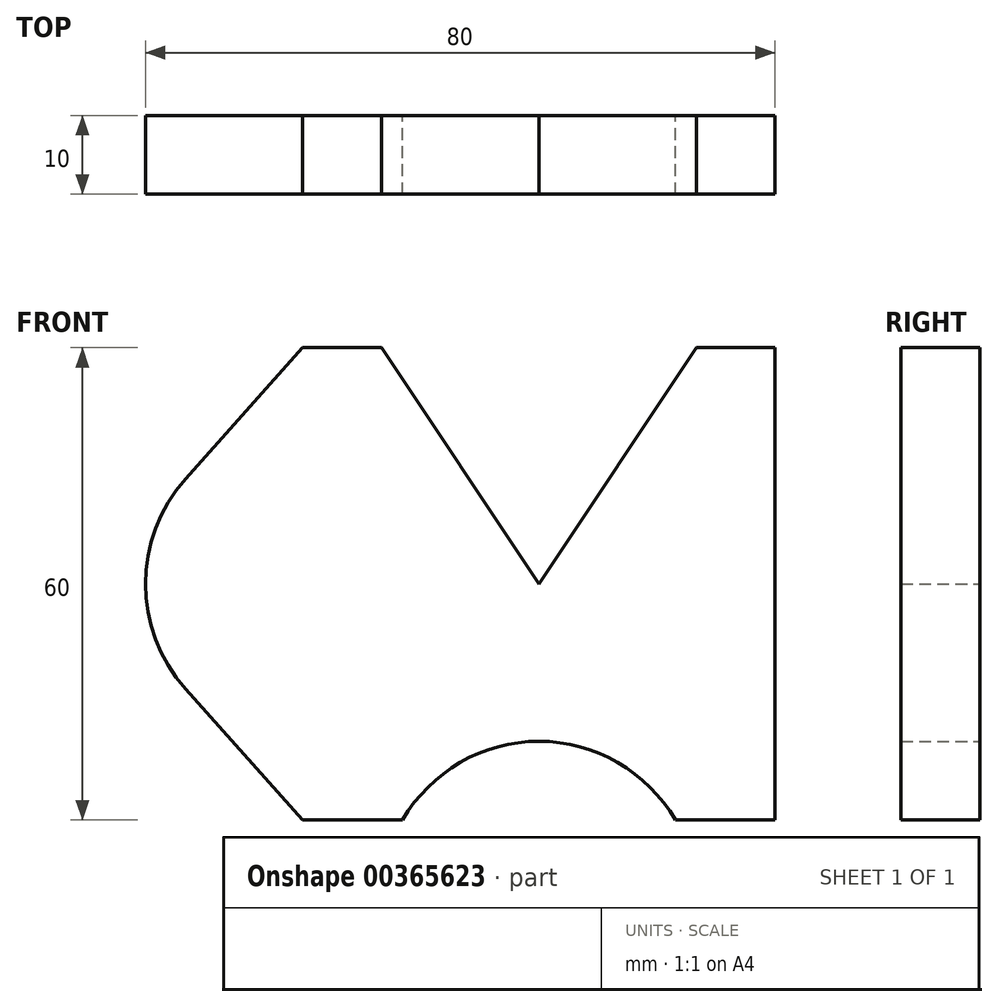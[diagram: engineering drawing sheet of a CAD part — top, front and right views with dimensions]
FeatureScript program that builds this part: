
annotation { "Feature Type Name" : "Feature", "Feature Type Description" : "" }
export const myFeature = defineFeature(function(context is Context, id is Id, definition is map)
    precondition{}
    {
        {
            var Q0;
            Q0=qCreatedBy(makeId("Front.planeOp"),FACE);
            var sketch = newSketch(context, id + "F0", { "sketchPlane" : qUnion([Q0])});
            skLineSegment(sketch, "E0", {"start": v(0, 0) * mm, "end": v(20, 30) * mm});
            skLineSegment(sketch, "E1", {"start": v(20, 30) * mm, "end": v(30, 30) * mm});
            skLineSegment(sketch, "E2", {"start": v(30, 30) * mm, "end": v(30, -30) * mm});
            skLineSegment(sketch, "E3", {"start": v(30, -30) * mm, "end": v(17.32, -30) * mm});
            skArc(sketch, "E4", {"start": v(17.32, -30) * mm, "mid": v(0, -20) * mm, "end": v(-17.32, -30) * mm});
            skLineSegment(sketch, "E5", {"start": v(-17.32, -30) * mm, "end": v(-30, -30) * mm});
            skLineSegment(sketch, "E6", {"start": v(-30, -30) * mm, "end": v(-44.9, -13.33) * mm});
            skLineSegment(sketch, "E7", {"start": v(0, 0) * mm, "end": v(-20, 30) * mm});
            skLineSegment(sketch, "E8", {"start": v(-20, 30) * mm, "end": v(-30, 30) * mm});
            skLineSegment(sketch, "E9", {"start": v(-30, 30) * mm, "end": v(-44.9, 13.33) * mm});
            skArc(sketch, "E10", {"start": v(-44.9, 13.33) * mm, "mid": v(-50, 0) * mm, "end": v(-44.9, -13.33) * mm});
            skLineSegment(sketch, "E11", {"start": v(-30, 30) * mm, "end": v(-30, -30) * mm, "construction": true});
            skSolve(sketch);
        }
        {
            var Q0;
            Q0=makeQuery(id+"F0.imprint","IMPRINT",FACE,{"disambiguationData":[TD([[makeQuery(id+"F0.imprint","IMPRINT",EDGE,{"derivedFrom":sQuery(id+"F0.wireOp",EDGE,"E0")}),-1.0]])]});
            extrude(context, id + "F1", {"entities" : qUnion([Q0]), "depth" : 10 * mm});
        }
    });
